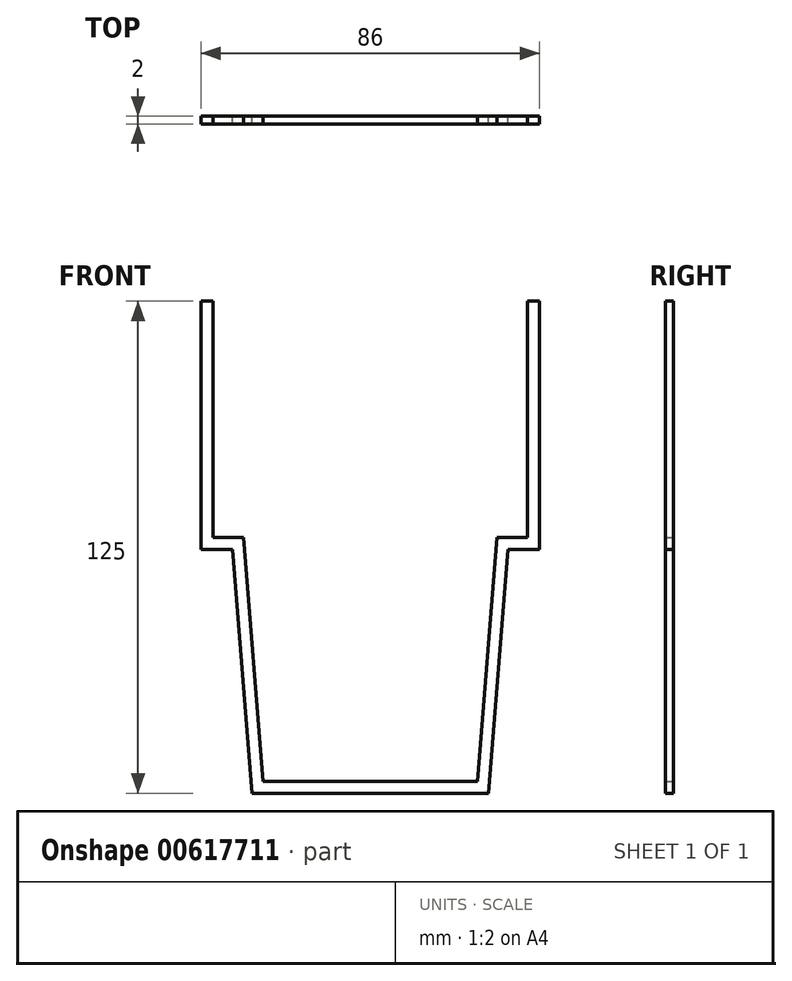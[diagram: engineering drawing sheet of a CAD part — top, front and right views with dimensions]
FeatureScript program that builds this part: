
annotation { "Feature Type Name" : "Feature", "Feature Type Description" : "" }
export const myFeature = defineFeature(function(context is Context, id is Id, definition is map)
    precondition{}
    {
        {
            var Q0;
            Q0=qCreatedBy(makeId("Front.planeOp"),FACE);
            var sketch = newSketch(context, id + "F0", { "sketchPlane" : qUnion([Q0])});
            skLineSegment(sketch, "E0", {"start": v(0, 0) * mm, "end": v(30, 0) * mm});
            skLineSegment(sketch, "E1", {"start": v(30, 0) * mm, "end": v(35, 62) * mm});
            skLineSegment(sketch, "E2", {"start": v(35, 62) * mm, "end": v(43, 62) * mm});
            skLineSegment(sketch, "E3", {"start": v(43, 62) * mm, "end": v(43, 125) * mm});
            skLineSegment(sketch, "E4", {"start": v(0, 0) * mm, "end": v(0, 3) * mm});
            skLineSegment(sketch, "E5", {"start": v(0, 3) * mm, "end": v(27.23, 3) * mm});
            skLineSegment(sketch, "E6", {"start": v(27.23, 3) * mm, "end": v(32.23, 65) * mm});
            skLineSegment(sketch, "E7", {"start": v(32.23, 65) * mm, "end": v(40, 65) * mm});
            skLineSegment(sketch, "E8", {"start": v(40, 65) * mm, "end": v(40, 125) * mm});
            skLineSegment(sketch, "E9", {"start": v(40, 125) * mm, "end": v(43, 125) * mm});
            skSolve(sketch);
        }
        {
            var Q0;
            Q0 = qSketchRegion(id + "F0", true);
            extrude(context, id + "F1", {"entities" : qUnion([Q0]), "depth" : 2 * mm, "offsetDistance" : 25 * mm});
        }
        {
            var Q0;
            Q0=makeQuery(id+"F1.opExtrude","SWEPT_BODY",BODY,{"disambiguationData":[OSD([sQuery(id+"F0.wireOp",EDGE,"E0"),sQuery(id+"F0.wireOp",EDGE,"E1"),sQuery(id+"F0.wireOp",EDGE,"E2"),sQuery(id+"F0.wireOp",EDGE,"E3"),sQuery(id+"F0.wireOp",EDGE,"E4"),sQuery(id+"F0.wireOp",EDGE,"E5"),sQuery(id+"F0.wireOp",EDGE,"E6"),sQuery(id+"F0.wireOp",EDGE,"E7"),sQuery(id+"F0.wireOp",EDGE,"E8"),sQuery(id+"F0.wireOp",EDGE,"E9")])]});
            var Q1;
            Q1=qCreatedBy(makeId("Right.planeOp"),FACE);
            mirror(context, id + "F2", {"operationType" : NewBodyOperationType.ADD, "entities" : qUnion([Q0]), "mirrorPlane" : qUnion([Q1])});
        }
    });
